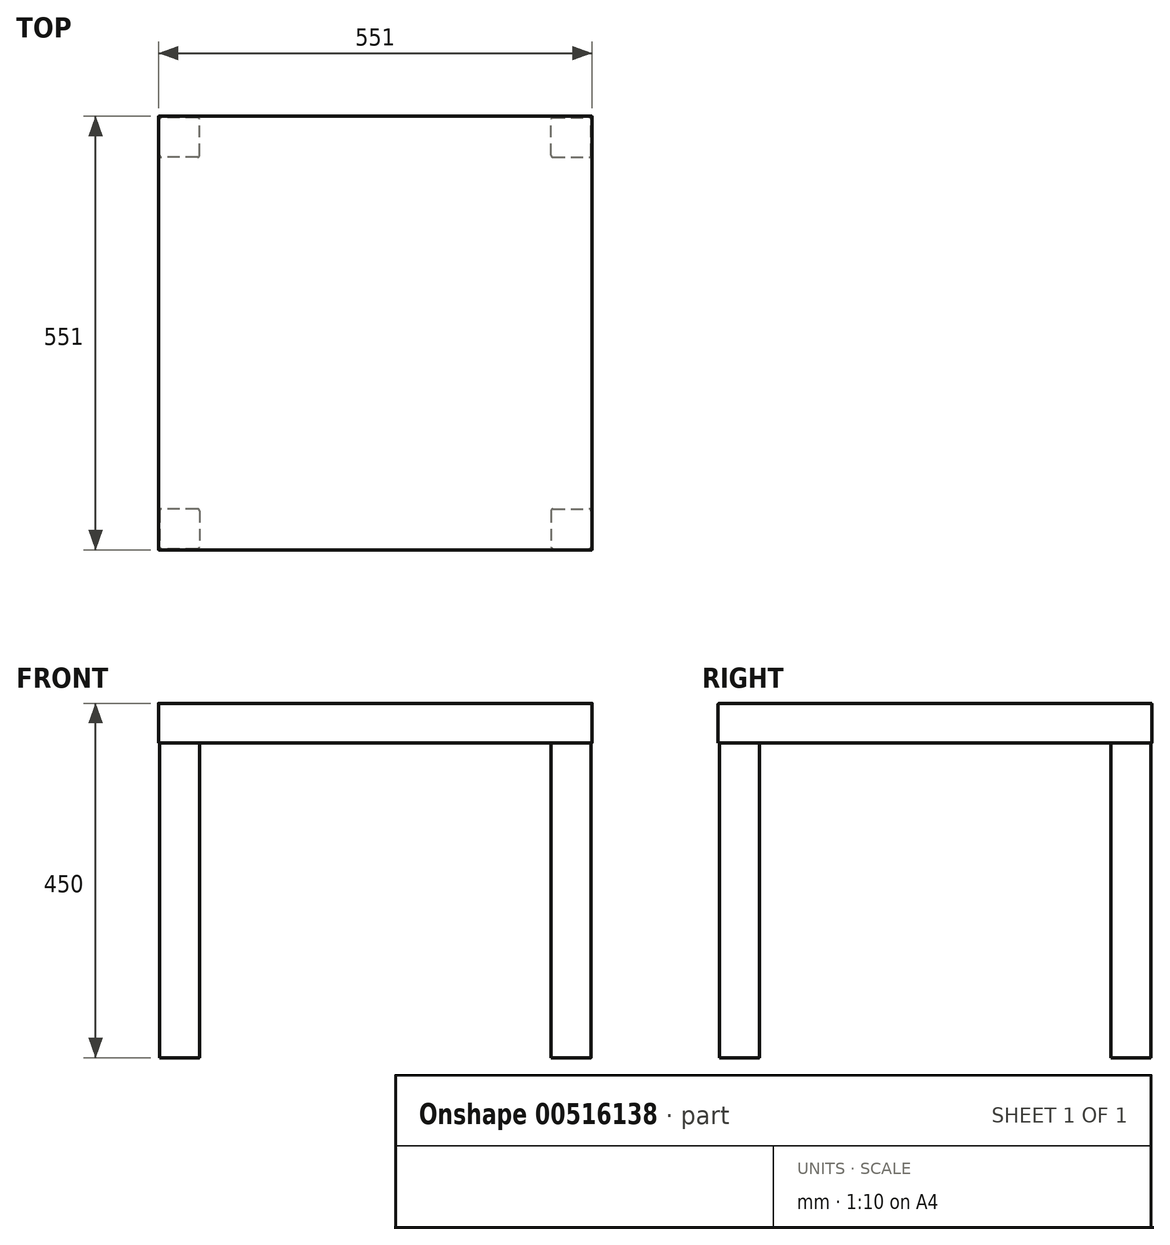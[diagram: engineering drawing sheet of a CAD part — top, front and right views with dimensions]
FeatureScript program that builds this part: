
annotation { "Feature Type Name" : "Feature", "Feature Type Description" : "" }
export const myFeature = defineFeature(function(context is Context, id is Id, definition is map)
    precondition{}
    {
        {
            assignVariable(context, id + "F0", {"name" : "TopHeight", "anyValue" : 50.1 * mm});
        }
        {
            var Q0;
            Q0=qCreatedBy(makeId("Top.planeOp"),FACE);
            var sketch = newSketch(context, id + "F1", { "sketchPlane" : qUnion([Q0])});
            skLineSegment(sketch, "E0.bottom", {"start": v(275.5, -275.5) * mm, "end": v(-275.5, -275.5) * mm});
            skLineSegment(sketch, "E0.top", {"start": v(275.5, 275.5) * mm, "end": v(-275.5, 275.5) * mm});
            skLineSegment(sketch, "E0.left", {"start": v(275.5, -275.5) * mm, "end": v(275.5, 275.5) * mm});
            skLineSegment(sketch, "E0.right", {"start": v(-275.5, -275.5) * mm, "end": v(-275.5, 275.5) * mm});
            skPoint(sketch, "E0.middle", {"position": v(0, 0) * mm});
            skLineSegment(sketch, "E1.bottom", {"start": v(-274, 274) * mm, "end": v(-223.3, 274) * mm});
            skLineSegment(sketch, "E1.top", {"start": v(-274, 223.3) * mm, "end": v(-223.3, 223.3) * mm});
            skLineSegment(sketch, "E1.left", {"start": v(-274, 274) * mm, "end": v(-274, 223.3) * mm});
            skLineSegment(sketch, "E1.right", {"start": v(-223.3, 274) * mm, "end": v(-223.3, 223.3) * mm});
            skLineSegment(sketch, "E2", {"start": v(0, 275.5) * mm, "end": v(0, -275.5) * mm, "construction": true});
            skLineSegment(sketch, "E3", {"start": v(-275.5, 0) * mm, "end": v(275.5, 0) * mm, "construction": true});
            skLineSegment(sketch, "E4.MirrorCS", {"start": v(223.3, 274) * mm, "end": v(223.3, 223.3) * mm});
            skLineSegment(sketch, "E5.MirrorCS", {"start": v(274, 274) * mm, "end": v(274, 223.3) * mm});
            skLineSegment(sketch, "E6.MirrorCS", {"start": v(274, 274) * mm, "end": v(223.3, 274) * mm});
            skLineSegment(sketch, "E7.MirrorCS", {"start": v(274, 223.3) * mm, "end": v(223.3, 223.3) * mm});
            skLineSegment(sketch, "E8.MirrorCS", {"start": v(274, -274) * mm, "end": v(274, -223.3) * mm});
            skLineSegment(sketch, "E9.MirrorCS", {"start": v(275.5, 275.5) * mm, "end": v(275.5, -275.5) * mm});
            skLineSegment(sketch, "E10.MirrorCS", {"start": v(274, -223.3) * mm, "end": v(223.3, -223.3) * mm});
            skLineSegment(sketch, "E11.MirrorCS", {"start": v(274, -274) * mm, "end": v(223.3, -274) * mm});
            skLineSegment(sketch, "E12.MirrorCS", {"start": v(223.3, -274) * mm, "end": v(223.3, -223.3) * mm});
            skLineSegment(sketch, "E13.MirrorCS", {"start": v(-275.5, 275.5) * mm, "end": v(-275.5, -275.5) * mm});
            skLineSegment(sketch, "E14.MirrorCS", {"start": v(-274, -274) * mm, "end": v(-223.3, -274) * mm});
            skLineSegment(sketch, "E15.MirrorCS", {"start": v(0, -275.5) * mm, "end": v(0, 275.5) * mm, "construction": true});
            skLineSegment(sketch, "E16.MirrorCS", {"start": v(-223.3, -274) * mm, "end": v(-223.3, -223.3) * mm});
            skLineSegment(sketch, "E17.MirrorCS", {"start": v(-274, -274) * mm, "end": v(-274, -223.3) * mm});
            skLineSegment(sketch, "E18.MirrorCS", {"start": v(-274, -223.3) * mm, "end": v(-223.3, -223.3) * mm});
            skSolve(sketch);
        }
        {
            var Q0;
            Q0=makeQuery(id+"F1.imprint","IMPRINT",FACE,{"disambiguationData":[TD([[makeQuery(id+"F1.imprint","IMPRINT",EDGE,{"derivedFrom":sQuery(id+"F1.wireOp",EDGE,"E0.top")}),1.0]])]});
            var Q1;
            Q1=makeQuery(id+"F1.imprint","IMPRINT",FACE,{"disambiguationData":[TD([[makeQuery(id+"F1.imprint","IMPRINT",EDGE,{"derivedFrom":sQuery(id+"F1.wireOp",EDGE,"E1.bottom")}),-1.0]])]});
            var Q2;
            Q2=makeQuery(id+"F1.imprint","IMPRINT",FACE,{"disambiguationData":[TD([[makeQuery(id+"F1.imprint","IMPRINT",EDGE,{"derivedFrom":sQuery(id+"F1.wireOp",EDGE,"E4.MirrorCS")}),1.0]])]});
            var Q3;
            Q3=makeQuery(id+"F1.imprint","IMPRINT",FACE,{"disambiguationData":[TD([[makeQuery(id+"F1.imprint","IMPRINT",EDGE,{"derivedFrom":sQuery(id+"F1.wireOp",EDGE,"E14.MirrorCS")}),1.0]])]});
            var Q4;
            Q4=makeQuery(id+"F1.imprint","IMPRINT",FACE,{"disambiguationData":[TD([[makeQuery(id+"F1.imprint","IMPRINT",EDGE,{"derivedFrom":sQuery(id+"F1.wireOp",EDGE,"E8.MirrorCS")}),1.0]])]});
            extrude(context, id + "F2", {"entities" : qUnion([Q0, Q1, Q2, Q3, Q4]), "oppositeDirection" : true, "depth" : getVariable(context, 'TopHeight'), "offsetDistance" : 25 * mm});
        }
        {
            var Q0;
            Q0=makeQuery(id+"F2.opExtrude","SWEPT_BODY",BODY,{"disambiguationData":[OSD([sQuery(id+"F1.wireOp",EDGE,"E0.top"),sQuery(id+"F1.wireOp",EDGE,"E9.MirrorCS"),sQuery(id+"F1.wireOp",EDGE,"E0.bottom"),sQuery(id+"F1.wireOp",EDGE,"E13.MirrorCS")])]});
            transform(context, id + "F3", {"entities" : qUnion([Q0]), "transformType" : TransformType.TRANSLATION_3D, "dx" : 0 * mm, "dy" : 0 * mm, "dz" : 450 * mm, "makeCopy" : false});
        }
        {
            var Q0;
            Q0=makeQuery(id+"F1.imprint","IMPRINT",FACE,{"disambiguationData":[TD([[makeQuery(id+"F1.imprint","IMPRINT",EDGE,{"derivedFrom":sQuery(id+"F1.wireOp",EDGE,"E1.bottom")}),-1.0]])]});
            var Q1;
            Q1=makeQuery(id+"F1.imprint","IMPRINT",FACE,{"disambiguationData":[TD([[makeQuery(id+"F1.imprint","IMPRINT",EDGE,{"derivedFrom":sQuery(id+"F1.wireOp",EDGE,"E8.MirrorCS")}),1.0]])]});
            var Q2;
            Q2=makeQuery(id+"F1.imprint","IMPRINT",FACE,{"disambiguationData":[TD([[makeQuery(id+"F1.imprint","IMPRINT",EDGE,{"derivedFrom":sQuery(id+"F1.wireOp",EDGE,"E14.MirrorCS")}),1.0]])]});
            var Q3;
            Q3=makeQuery(id+"F1.imprint","IMPRINT",FACE,{"disambiguationData":[TD([[makeQuery(id+"F1.imprint","IMPRINT",EDGE,{"derivedFrom":sQuery(id+"F1.wireOp",EDGE,"E4.MirrorCS")}),1.0]])]});
            extrude(context, id + "F4", {"entities" : qUnion([Q0, Q1, Q2, Q3]), "operationType" : NewBodyOperationType.ADD, "depth" : 400 * mm, "offsetDistance" : 25 * mm});
        }
        {
            var Q0;
            Q0=makeQuery(id+"F4.opExtrude","SWEPT_EDGE",EDGE,{"disambiguationData":[OSD([sQuery(id+"F1.wireOp",EDGE,"E14.MirrorCS"),sQuery(id+"F1.wireOp",EDGE,"E17.MirrorCS")])]});
            var Q1;
            Q1=makeQuery(id+"F4.opExtrude","SWEPT_EDGE",EDGE,{"disambiguationData":[OSD([sQuery(id+"F1.wireOp",EDGE,"E1.top"),sQuery(id+"F1.wireOp",EDGE,"E1.left")])]});
            var Q2;
            Q2=makeQuery(id+"F4.opExtrude","SWEPT_EDGE",EDGE,{"disambiguationData":[OSD([sQuery(id+"F1.wireOp",EDGE,"E4.MirrorCS"),sQuery(id+"F1.wireOp",EDGE,"E7.MirrorCS")])]});
            var Q3;
            Q3=makeQuery(id+"F4.opExtrude","SWEPT_EDGE",EDGE,{"disambiguationData":[OSD([sQuery(id+"F1.wireOp",EDGE,"E11.MirrorCS"),sQuery(id+"F1.wireOp",EDGE,"E12.MirrorCS")])]});
            var Q4;
            Q4=makeQuery(id+"F4.opExtrude","SWEPT_EDGE",EDGE,{"disambiguationData":[OSD([sQuery(id+"F1.wireOp",EDGE,"E14.MirrorCS"),sQuery(id+"F1.wireOp",EDGE,"E16.MirrorCS")])]});
            var Q5;
            Q5=makeQuery(id+"F4.opExtrude","SWEPT_EDGE",EDGE,{"disambiguationData":[OSD([sQuery(id+"F1.wireOp",EDGE,"E1.top"),sQuery(id+"F1.wireOp",EDGE,"E1.right")])]});
            var Q6;
            Q6=makeQuery(id+"F4.opExtrude","SWEPT_EDGE",EDGE,{"disambiguationData":[OSD([sQuery(id+"F1.wireOp",EDGE,"E8.MirrorCS"),sQuery(id+"F1.wireOp",EDGE,"E11.MirrorCS")])]});
            var Q7;
            Q7=makeQuery(id+"F4.opExtrude","SWEPT_EDGE",EDGE,{"disambiguationData":[OSD([sQuery(id+"F1.wireOp",EDGE,"E5.MirrorCS"),sQuery(id+"F1.wireOp",EDGE,"E7.MirrorCS")])]});
            var Q8;
            Q8=makeQuery(id+"F4.opExtrude","SWEPT_EDGE",EDGE,{"disambiguationData":[OSD([sQuery(id+"F1.wireOp",EDGE,"E16.MirrorCS"),sQuery(id+"F1.wireOp",EDGE,"E18.MirrorCS")])]});
            var Q9;
            Q9=makeQuery(id+"F4.opExtrude","SWEPT_EDGE",EDGE,{"disambiguationData":[OSD([sQuery(id+"F1.wireOp",EDGE,"E8.MirrorCS"),sQuery(id+"F1.wireOp",EDGE,"E10.MirrorCS")])]});
            var Q10;
            Q10=makeQuery(id+"F4.opExtrude","SWEPT_EDGE",EDGE,{"disambiguationData":[OSD([sQuery(id+"F1.wireOp",EDGE,"E1.bottom"),sQuery(id+"F1.wireOp",EDGE,"E1.right")])]});
            var Q11;
            Q11=makeQuery(id+"F4.opExtrude","SWEPT_EDGE",EDGE,{"disambiguationData":[OSD([sQuery(id+"F1.wireOp",EDGE,"E5.MirrorCS"),sQuery(id+"F1.wireOp",EDGE,"E6.MirrorCS")])]});
            var Q12;
            Q12=makeQuery(id+"F4.opExtrude","SWEPT_EDGE",EDGE,{"disambiguationData":[OSD([sQuery(id+"F1.wireOp",EDGE,"E10.MirrorCS"),sQuery(id+"F1.wireOp",EDGE,"E12.MirrorCS")])]});
            var Q13;
            Q13=makeQuery(id+"F4.opExtrude","SWEPT_EDGE",EDGE,{"disambiguationData":[OSD([sQuery(id+"F1.wireOp",EDGE,"E17.MirrorCS"),sQuery(id+"F1.wireOp",EDGE,"E18.MirrorCS")])]});
            var Q14;
            Q14=makeQuery(id+"F4.opExtrude","SWEPT_EDGE",EDGE,{"disambiguationData":[OSD([sQuery(id+"F1.wireOp",EDGE,"E4.MirrorCS"),sQuery(id+"F1.wireOp",EDGE,"E6.MirrorCS")])]});
            var Q15;
            Q15=makeQuery(id+"F4.opExtrude","SWEPT_EDGE",EDGE,{"disambiguationData":[OSD([sQuery(id+"F1.wireOp",EDGE,"E1.bottom"),sQuery(id+"F1.wireOp",EDGE,"E1.left")])]});
            fillet(context, id + "F5", {"entities" : qUnion([Q0, Q1, Q2, Q3, Q4, Q5, Q6, Q7, Q8, Q9, Q10, Q11, Q12, Q13, Q14, Q15]), "radius" : 2.5 * mm, "tangentPropagation" : true, "allowEdgeOverflow" : false});
        }
        {
            var Q0;
            Q0=makeQuery(id+"F2.opExtrude","CAP_EDGE",EDGE,{"disambiguationData":[OSD([sQuery(id+"F1.wireOp",EDGE,"E0.bottom")])],"isStart":true});
            var Q1;
            Q1=makeQuery(id+"F2.opExtrude","CAP_EDGE",EDGE,{"disambiguationData":[OSD([sQuery(id+"F1.wireOp",EDGE,"E9.MirrorCS")])],"isStart":true});
            var Q2;
            Q2=makeQuery(id+"F2.opExtrude","CAP_EDGE",EDGE,{"disambiguationData":[OSD([sQuery(id+"F1.wireOp",EDGE,"E13.MirrorCS")])],"isStart":true});
            var Q3;
            Q3=makeQuery(id+"F2.opExtrude","CAP_EDGE",EDGE,{"disambiguationData":[OSD([sQuery(id+"F1.wireOp",EDGE,"E0.top")])],"isStart":true});
            var Q4;
            Q4=makeQuery(id+"F2.opExtrude","SWEPT_EDGE",EDGE,{"disambiguationData":[OSD([sQuery(id+"F1.wireOp",EDGE,"E9.MirrorCS"),sQuery(id+"F1.wireOp",EDGE,"E0.bottom")])]});
            var Q5;
            Q5=makeQuery(id+"F2.opExtrude","SWEPT_EDGE",EDGE,{"disambiguationData":[OSD([sQuery(id+"F1.wireOp",EDGE,"E0.bottom"),sQuery(id+"F1.wireOp",EDGE,"E13.MirrorCS")])]});
            var Q6;
            Q6=makeQuery(id+"F2.opExtrude","SWEPT_EDGE",EDGE,{"disambiguationData":[OSD([sQuery(id+"F1.wireOp",EDGE,"E0.top"),sQuery(id+"F1.wireOp",EDGE,"E9.MirrorCS")])]});
            var Q7;
            Q7=makeQuery(id+"F2.opExtrude","SWEPT_EDGE",EDGE,{"disambiguationData":[OSD([sQuery(id+"F1.wireOp",EDGE,"E0.top"),sQuery(id+"F1.wireOp",EDGE,"E13.MirrorCS")])]});
            fillet(context, id + "F6", {"entities" : qUnion([Q0, Q1, Q2, Q3, Q4, Q5, Q6, Q7]), "radius" : 1 * mm, "tangentPropagation" : true, "allowEdgeOverflow" : false});
        }
    });
